# Revit family: Partition_HDPE_CeilingHung_Metpar
name_source: partatom
category: Casework
units: mm (PartAtom-declared; Revit-internal decimal feet)

## family parameters
Always vertical = Yes
Cut with Voids When Loaded = No
Room Calculation Point = No
Shared = Yes
Work Plane-Based = No

## types (1)
- As Specified
    Assembly Code = C1010400
    Building Codes = http://www.metpar.com
    Ceiling Height = 9' - 0"
    Construction Details = http://www.arcat.com
    Default Elevation = 0' - 0"
    Description = Partition as Specified in 10 21 00
    Door Handle Height = 3' - 0"
    Door Height = 4' - 11"
    Door Thickness = 0' - 0 3/4"
    Expected Lifespan (Years) = 0
    GapHng = 0' - 0"
    GapStrk = 0' - 1 1/4"
    Green Building-LEED = http://www.arcat.com
    Has Door = Yes
    Has Wall extension = No
    Hinge Pilaster = Yes
    Hinge Side Panel = No
    HngPilast2 = 0' - 6"
    HngPnlOffset = 0' - 0"
    Installation-Fabrication = http://www.metpar.com
    Keynote = 10 21 00
    Maintenance Schedule (Months) = 0
    Manufacturer = Metpar Corp.
    Manufacturer Fax = 516-333-2618
    Manufacturer Website = http://www.metpar.com
    Model = Ceiling Hung
    Offset Hinge Panel = No
    Offset Strike Panel = Yes
    Panel Height = 4' - 11"
    Panel Height from Floor = 1' - 0"
    Panel Thickness = 0' - 0 1/2"
    Pilaster Thickness = 0' - 0 3/4"
    Pilaster Width_Hinge Side = 1' - 0"
    Pilaster Width_Strike Side = 0' - 7"
    Product Data = http://www.arcat.com
    Product Properties = http://www.arcat.com
    Revision = R1_04-2011
    Sales Information = http://www.metpar.com
    Send Message = http://www.arcat.com
    Specification = http://www.arcat.com
    Strike Pilaster = Yes
    Strike Side Panel = Yes
    StrkPilast2 = 0' - 3 1/2"
    StrkPnlOffset = 0' - 3 1/4"
    Test Data = http://www.metpar.com
    Type Comments = Contact Manufacturer for More Information
    URL = http://www.metpar.com
    Unit Width = 3' - 0"
    Warranty Duration (Years) = 0
    offset = 0' - 5 3/4"

## geometry (parser evidence)
native form markers: Blend x10, Sweep x8
no freeform markers — native parametric forms only
